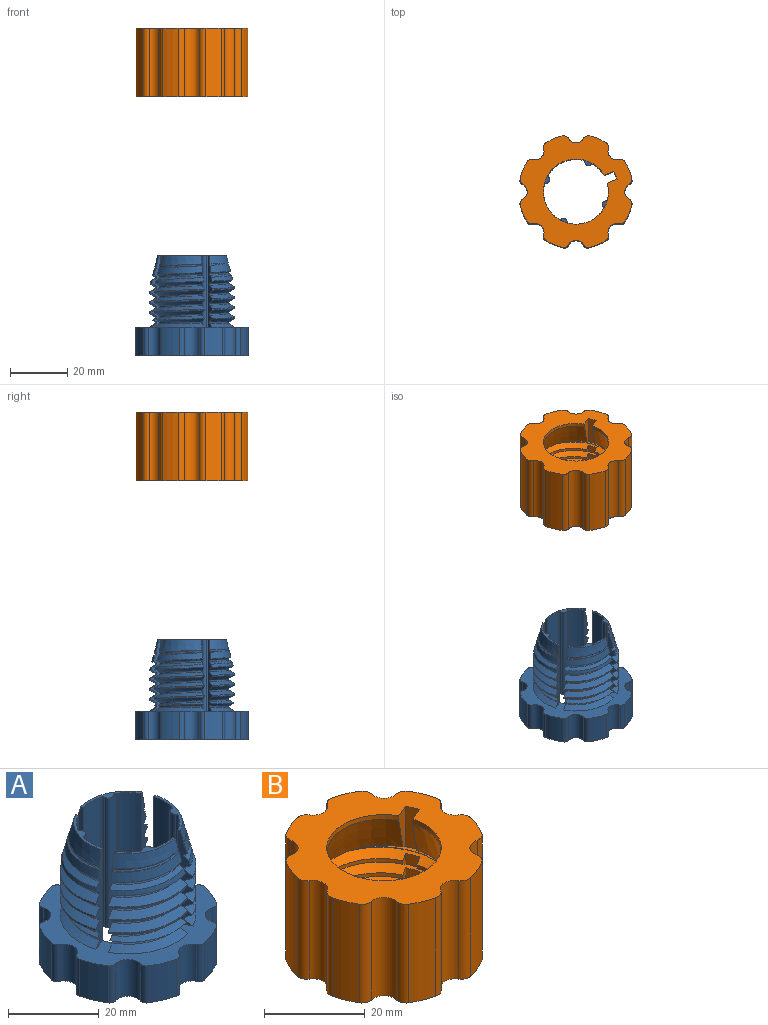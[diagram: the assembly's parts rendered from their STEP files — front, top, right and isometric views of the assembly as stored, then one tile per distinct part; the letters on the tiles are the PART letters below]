
ASSEMBLY  parts=2 mates=1
PART A: 173 faces, bbox 39.3x39.3x35 mm
  f0: cylinder r=11.39mm len=35mm, axis (0,0,-1), area 193.1mm2, adj f6,f127,f152,f166
  f1: cylinder r=11.39mm len=35mm, axis (0,0,-1), area 416.3mm2, adj f4,f5,f6,f127,f158,f159,f165,f168
  f2: cylinder r=11.39mm len=35mm, axis (0,0,-1), area 416.3mm2, adj f4,f5,f57,f127,f156,f157,f167,f170
  f3: cylinder r=11.39mm len=35mm, axis (0,0,-1), area 416.3mm2, adj f4,f57,f87,f127,f154,f155,f169,f172
  f4: plane 39.23x39.23mm, normal (0,0,1), area 475.3mm2, adj f1,f2,f3,f51,f52,f84,f112,f119
  f5: plane 13.6x6.3mm, normal (0,0,1), area 12mm2, adj f1,f2,f17,f157,f158,f163,f167,f168
  f6: plane 13.6x6.3mm, normal (0,0,1), area 12mm2, adj f0,f1,f18,f152,f159,f164,f165,f166
  f7: cylinder r=15mm len=17.54mm, axis (0,0,1), area 9mm2, adj f25,f45,f157,f158
  f8: cylinder r=15mm len=17.54mm, axis (0,0,1), area 7.3mm2, adj f26,f46,f116,f152,f159
  f9: cylinder r=15mm len=17.54mm, axis (0,0,1), area 9mm2, adj f23,f43,f157,f158
  f10: cylinder r=15mm len=17.54mm, axis (0,0,1), area 9mm2, adj f24,f44,f152,f159
  f11: cylinder r=15mm len=17.54mm, axis (0,0,1), area 9mm2, adj f21,f41,f157,f158
  f12: cylinder r=15mm len=17.54mm, axis (0,0,1), area 9mm2, adj f22,f42,f152,f159
  f13: cylinder r=11.39mm len=35mm, axis (0,0,-1), area 193.1mm2, adj f87,f127,f153,f171
  f14: cone r=12mm half-angle=15deg, axis (0,0,-1), area 24.3mm2, adj f27,f47,f157,f158
  f15: cone r=12mm half-angle=15deg, axis (0,0,-1), area 29.3mm2, adj f28,f48,f152,f159
  f16: cone r=12mm half-angle=15deg, axis (0,0,-1), area 43.1mm2, adj f39,f49,f70,f157,f158
  f17: cone r=12mm half-angle=15deg, axis (0,0,-1), area 56.2mm2, adj f5,f39,f83,f157,f158
  f18: cone r=12mm half-angle=15deg, axis (0,0,-1), area 95.4mm2, adj f6,f40,f50,f152,f159
  f19: bspline ~22.5x17.32mm, area 31.8mm2, adj f29,f55,f157,f158
  f20: bspline ~30.31x22.5mm, area 44.5mm2, adj f30,f56,f115,f152,f159
  f21: bspline ~17.54x8.87mm, area 44.9mm2, adj f11,f31,f157,f158
  f22: bspline ~30.31x22.5mm, area 44.9mm2, adj f12,f32,f152,f159
  f23: bspline ~17.54x8.87mm, area 44.9mm2, adj f9,f33,f157,f158
  f24: bspline ~30.31x22.5mm, area 44.9mm2, adj f10,f34,f152,f159
  f25: bspline ~22.5x17.32mm, area 44.9mm2, adj f7,f35,f157,f158
  f26: bspline ~30.31x22.5mm, area 44.3mm2, adj f8,f36,f116,f152,f159
  f27: bspline ~22.5x17.32mm, area 25.9mm2, adj f14,f37,f157,f158
  f28: bspline ~30.31x22.5mm, area 19.9mm2, adj f15,f38,f152,f159
  f29: bspline ~19.42x14.95mm, area 14.4mm2, adj f19,f41,f157,f158
  f30: bspline ~26.16x19.42mm, area 14.4mm2, adj f20,f42,f152,f159
  f31: bspline ~19.42x14.95mm, area 14.4mm2, adj f21,f43,f157,f158
  f32: bspline ~26.16x19.42mm, area 14.4mm2, adj f22,f44,f152,f159
  f33: bspline ~19.42x14.95mm, area 14.4mm2, adj f23,f45,f157,f158
  f34: bspline ~26.16x19.42mm, area 14.4mm2, adj f24,f46,f152,f159
  f35: bspline ~19.42x14.95mm, area 14.4mm2, adj f25,f47,f157,f158
  f36: bspline ~26.16x19.42mm, area 14.4mm2, adj f26,f48,f152,f159
  f37: bspline ~19.42x14.95mm, area 14.4mm2, adj f27,f49,f157,f158
  f38: bspline ~26.16x19.42mm, area 14.4mm2, adj f28,f50,f152,f159
  f39: bspline ~19.42x14.95mm, area 12.8mm2, adj f16,f17,f70,f83,f157,f158
  f40: bspline ~19.42x14.95mm, area 2.5mm2, adj f18,f159
  f41: bspline ~22.5x17.32mm, area 44.9mm2, adj f11,f29,f157,f158
  f42: bspline ~17.54x8.87mm, area 44.9mm2, adj f12,f30,f152,f159
  f43: bspline ~22.5x17.32mm, area 44.9mm2, adj f9,f31,f157,f158
  f44: bspline ~17.54x8.87mm, area 44.9mm2, adj f10,f32,f152,f159
  f45: bspline ~22.5x17.32mm, area 44.9mm2, adj f7,f33,f157,f158
  f46: bspline ~30.31x22.5mm, area 44.9mm2, adj f8,f34,f152,f159
  f47: bspline ~22.5x17.32mm, area 33.2mm2, adj f14,f35,f157,f158
  f48: bspline ~30.31x22.5mm, area 28.6mm2, adj f15,f36,f152,f159
  f49: bspline ~22.5x17.32mm, area 15.3mm2, adj f16,f37,f157,f158
  f50: bspline ~30.31x22.5mm, area 11mm2, adj f18,f38,f152,f159
  f51: cone r=15mm half-angle=60deg, axis (0,0,-1), area 44.9mm2, adj f4,f53,f157,f158
  f52: cone r=15mm half-angle=60deg, axis (0,0,-1), area 44.9mm2, adj f4,f54,f152,f159
  f53: torus R=13.15mm, axis (0,0,1), area 14.4mm2, adj f51,f55,f157,f158
  f54: torus R=13.15mm, axis (0,0,1), area 13mm2, adj f52,f56,f117,f152,f159
  f55: cone r=12.95mm half-angle=60deg, axis (0,0,1), area 31.8mm2, adj f19,f53,f157,f158
  f56: cone r=12.95mm half-angle=60deg, axis (0,0,1), area 35.1mm2, adj f20,f54,f115,f118,f159
  f57: plane 13.6x6.3mm, normal (0,0,1), area 12mm2, adj f2,f3,f63,f155,f156,f162,f169,f170
  f58: cylinder r=15mm len=17.54mm, axis (0,0,1), area 9mm2, adj f67,f79,f155,f156
  f59: cylinder r=15mm len=17.54mm, axis (0,0,1), area 9mm2, adj f66,f78,f155,f156
  f60: cylinder r=15mm len=17.54mm, axis (0,0,1), area 9mm2, adj f65,f77,f155,f156
  f61: cone r=12mm half-angle=15deg, axis (0,0,-1), area 19.1mm2, adj f68,f80,f155,f156
  f62: cone r=12mm half-angle=15deg, axis (0,0,-1), area 38.7mm2, adj f69,f81,f155,f156
  f63: cone r=12mm half-angle=15deg, axis (0,0,-1), area 69.4mm2, adj f57,f82,f155,f156
  f64: bspline ~30.31x22.5mm, area 15mm2, adj f71,f86,f155,f156
  f65: bspline ~30.31x22.5mm, area 44.9mm2, adj f60,f72,f155,f156
  f66: bspline ~30.31x22.5mm, area 44.9mm2, adj f59,f73,f155,f156
  f67: bspline ~30.31x22.5mm, area 44.9mm2, adj f58,f74,f155,f156
  f68: bspline ~30.31x22.5mm, area 32.2mm2, adj f61,f75,f155,f156
  f69: bspline ~30.31x22.5mm, area 8.1mm2, adj f62,f76,f155,f156
  f70: bspline ~22.5x17.32mm, area 2.4mm2, adj f16,f39,f157
  f71: bspline ~26.16x19.42mm, area 14.4mm2, adj f64,f77,f155,f156
  f72: bspline ~26.16x19.42mm, area 14.4mm2, adj f65,f78,f155,f156
  f73: bspline ~26.16x19.42mm, area 14.4mm2, adj f66,f79,f155,f156
  f74: bspline ~26.16x19.42mm, area 14.4mm2, adj f67,f80,f155,f156
  f75: bspline ~26.16x19.42mm, area 14.4mm2, adj f68,f81,f155,f156
  f76: bspline ~26.16x19.42mm, area 14.4mm2, adj f69,f82,f155,f156
  f77: bspline ~30.31x22.5mm, area 44.9mm2, adj f60,f71,f155,f156
  f78: bspline ~30.31x22.5mm, area 44.9mm2, adj f59,f72,f155,f156
  f79: bspline ~30.31x22.5mm, area 44.9mm2, adj f58,f73,f155,f156
  f80: bspline ~30.31x22.5mm, area 37.9mm2, adj f61,f74,f155,f156
  f81: bspline ~30.31x22.5mm, area 19.7mm2, adj f62,f75,f155,f156
  f82: bspline ~30.31x22.5mm, area 2.6mm2, adj f63,f76,f155,f156
  f83: bspline ~12.99x8.53mm, area 0mm2, adj f17,f39,f157
  f84: cone r=15mm half-angle=60deg, axis (0,0,-1), area 44.9mm2, adj f4,f85,f155,f156
  f85: torus R=13.15mm, axis (0,0,1), area 14.4mm2, adj f84,f86,f155,f156
  f86: cone r=12.95mm half-angle=60deg, axis (0,0,1), area 15mm2, adj f64,f85,f155,f156
  f87: plane 13.6x6.3mm, normal (0,0,1), area 12mm2, adj f3,f13,f93,f153,f154,f161,f171,f172
  f88: cylinder r=15mm len=17.54mm, axis (0,0,1), area 9mm2, adj f97,f108,f153,f154
  f89: cylinder r=15mm len=17.54mm, axis (0,0,1), area 9mm2, adj f96,f107,f153,f154
  f90: cylinder r=15mm len=17.54mm, axis (0,0,1), area 9mm2, adj f95,f106,f153,f154
  f91: cone r=12mm half-angle=15deg, axis (0,0,-1), area 13.6mm2, adj f98,f109,f153,f154
  f92: cone r=12mm half-angle=15deg, axis (0,0,-1), area 34.2mm2, adj f99,f110,f153,f154
  f93: cone r=12mm half-angle=15deg, axis (0,0,-1), area 83.2mm2, adj f87,f111,f153,f154
  f94: bspline ~15x6.11mm, area 1.3mm2, adj f100,f114,f154
  f95: bspline ~22.5x17.32mm, area 44.9mm2, adj f90,f101,f153,f154
  f96: bspline ~22.5x17.32mm, area 44.9mm2, adj f89,f102,f153,f154
  f97: bspline ~22.5x17.32mm, area 44.9mm2, adj f88,f103,f153,f154
  f98: bspline ~22.5x17.32mm, area 38.5mm2, adj f91,f104,f153,f154
  f99: bspline ~22.5x17.32mm, area 13.9mm2, adj f92,f105,f153,f154
  f100: bspline ~19.42x14.95mm, area 13.1mm2, adj f94,f106,f113,f153,f154
  f101: bspline ~19.42x14.95mm, area 14.4mm2, adj f95,f107,f153,f154
  f102: bspline ~19.42x14.95mm, area 14.4mm2, adj f96,f108,f153,f154
  f103: bspline ~19.42x14.95mm, area 14.4mm2, adj f97,f109,f153,f154
  f104: bspline ~19.42x14.95mm, area 14.4mm2, adj f98,f110,f153,f154
  f105: bspline ~19.42x14.95mm, area 14.4mm2, adj f99,f111,f153,f154
  f106: bspline ~22.5x17.32mm, area 44.9mm2, adj f90,f100,f153,f154
  f107: bspline ~22.5x17.32mm, area 44.9mm2, adj f89,f101,f153,f154
  f108: bspline ~22.5x17.32mm, area 44.9mm2, adj f88,f102,f153,f154
  f109: bspline ~22.5x17.32mm, area 42.6mm2, adj f91,f103,f153,f154
  f110: bspline ~22.5x17.32mm, area 24.1mm2, adj f92,f104,f153,f154
  f111: bspline ~22.5x17.32mm, area 6.7mm2, adj f93,f105,f153,f154
  f112: cone r=15mm half-angle=60deg, axis (0,0,-1), area 44.9mm2, adj f4,f113,f153,f154
  f113: torus R=13.15mm, axis (0,0,1), area 13mm2, adj f100,f112,f114,f153,f154
  f114: cone r=12.95mm half-angle=60deg, axis (0,0,1), area 1.3mm2, adj f94,f113,f154
  f115: cylinder r=15mm len=14.84mm, axis (0,0,1), area 4.4mm2, adj f20,f56,f118,f152
  f116: cone r=12mm half-angle=15deg, axis (0,0,-1), area 2.1mm2, adj f8,f26,f152
  f117: bspline ~11.21x6.62mm, area 1.6mm2, adj f54,f118,f152
  f118: bspline ~12.99x8.53mm, area 9.4mm2, adj f56,f115,f117,f152
  f119: cylinder r=20.07mm len=10mm, axis (0,0,1), area 69.1mm2, adj f4,f127,f136,f151
  f120: cylinder r=20.07mm len=10mm, axis (0,0,1), area 69.1mm2, adj f4,f127,f137,f138
  f121: cylinder r=20.07mm len=10mm, axis (0,0,1), area 69.1mm2, adj f4,f127,f139,f140
  f122: cylinder r=20.07mm len=10mm, axis (0,0,1), area 69.1mm2, adj f4,f127,f141,f142
  f123: cylinder r=20.07mm len=10mm, axis (0,0,1), area 69.1mm2, adj f4,f127,f143,f144
  f124: cylinder r=20.07mm len=10mm, axis (0,0,1), area 69.1mm2, adj f4,f127,f145,f146
  f125: cylinder r=20.07mm len=10mm, axis (0,0,1), area 69.1mm2, adj f4,f127,f147,f148
  f126: cylinder r=20.07mm len=10mm, axis (0,0,1), area 69.1mm2, adj f4,f127,f149,f150
  f127: plane 39.23x39.23mm, normal (0,0,-1), area 741.6mm2, adj f0,f1,f2,f3,f13,f119,f120,f121
  f128: cylinder r=3mm len=10mm, axis (0,0,-1), area 67.5mm2, adj f4,f127,f150,f151
  f129: cylinder r=3mm len=10mm, axis (0,0,-1), area 67.5mm2, adj f4,f127,f148,f149
  f130: cylinder r=3mm len=10mm, axis (0,0,-1), area 67.5mm2, adj f4,f127,f146,f147
  f131: cylinder r=3mm len=10mm, axis (0,0,-1), area 67.5mm2, adj f4,f127,f144,f145
  f132: cylinder r=3mm len=10mm, axis (0,0,-1), area 67.5mm2, adj f4,f127,f142,f143
  f133: cylinder r=3mm len=10mm, axis (0,0,-1), area 67.5mm2, adj f4,f127,f140,f141
  f134: cylinder r=3mm len=10mm, axis (0,0,-1), area 67.5mm2, adj f4,f127,f138,f139
  f135: cylinder r=3mm len=10mm, axis (0,0,-1), area 67.5mm2, adj f4,f127,f136,f137
  f136: cylinder r=1.5mm len=10mm, axis (0,0,-1), area 20.2mm2, adj f4,f119,f127,f135
  f137: cylinder r=1.5mm len=10mm, axis (0,0,1), area 20.2mm2, adj f4,f120,f127,f135
  f138: cylinder r=1.5mm len=10mm, axis (0,0,-1), area 20.2mm2, adj f4,f120,f127,f134
  f139: cylinder r=1.5mm len=10mm, axis (0,0,1), area 20.2mm2, adj f4,f121,f127,f134
  f140: cylinder r=1.5mm len=10mm, axis (0,0,-1), area 20.2mm2, adj f4,f121,f127,f133
  f141: cylinder r=1.5mm len=10mm, axis (0,0,1), area 20.2mm2, adj f4,f122,f127,f133
  f142: cylinder r=1.5mm len=10mm, axis (0,0,-1), area 20.2mm2, adj f4,f122,f127,f132
  f143: cylinder r=1.5mm len=10mm, axis (0,0,1), area 20.2mm2, adj f4,f123,f127,f132
  f144: cylinder r=1.5mm len=10mm, axis (0,0,-1), area 20.2mm2, adj f4,f123,f127,f131
  f145: cylinder r=1.5mm len=10mm, axis (0,0,1), area 20.2mm2, adj f4,f124,f127,f131
  f146: cylinder r=1.5mm len=10mm, axis (0,0,-1), area 20.2mm2, adj f4,f124,f127,f130
  f147: cylinder r=1.5mm len=10mm, axis (0,0,1), area 20.2mm2, adj f4,f125,f127,f130
  f148: cylinder r=1.5mm len=10mm, axis (0,0,-1), area 20.2mm2, adj f4,f125,f127,f129
  f149: cylinder r=1.5mm len=10mm, axis (0,0,1), area 20.2mm2, adj f4,f126,f127,f129
  f150: cylinder r=1.5mm len=10mm, axis (0,0,-1), area 20.2mm2, adj f4,f126,f127,f128
  f151: cylinder r=1.5mm len=10mm, axis (0,0,1), area 20.2mm2, adj f4,f119,f127,f128
  f152: plane 35.05x3.48mm, normal (-0.38,0.92,0), area 91.6mm2, adj f0,f4,f6,f8,f10,f12,f15,f18
  f153: plane 35.05x3.48mm, normal (0.38,-0.92,0), area 91.4mm2, adj f4,f13,f87,f88,f89,f90,f91,f92
  f154: plane 25.05x3.41mm, normal (-0.92,-0.38,0), area 53.5mm2, adj f3,f4,f87,f88,f89,f90,f91,f92
  f155: plane 25.05x3.41mm, normal (0.92,0.38,0), area 53.5mm2, adj f3,f4,f57,f58,f59,f60,f61,f62
  f156: plane 25.05x3.41mm, normal (0.38,-0.92,0), area 53.3mm2, adj f2,f4,f57,f58,f59,f60,f61,f62
  f157: plane 25.05x3.41mm, normal (-0.38,0.92,0), area 53.4mm2, adj f2,f4,f5,f7,f9,f11,f14,f16
  f158: plane 25.05x3.41mm, normal (0.92,0.38,0), area 53.8mm2, adj f1,f4,f5,f7,f9,f11,f14,f16
  f159: plane 25.05x3.41mm, normal (-0.92,-0.38,0), area 53.9mm2, adj f1,f4,f6,f8,f10,f12,f15,f18
  f160: plane 10x2.77mm, normal (-0.92,-0.38,0), area 30mm2, adj f4,f127,f152,f153
  f161: cylinder r=1.25mm len=35mm, axis (0,0,-1), area 96.6mm2, adj f87,f127,f171,f172
  f162: cylinder r=1.25mm len=35mm, axis (0,0,-1), area 96.6mm2, adj f57,f127,f169,f170
  f163: cylinder r=1.25mm len=35mm, axis (0,0,-1), area 96.6mm2, adj f5,f127,f167,f168
  f164: cylinder r=1.25mm len=35mm, axis (0,0,-1), area 96.6mm2, adj f6,f127,f165,f166
  f165: cylinder r=0.75mm len=35mm, axis (0,0,-1), area 33.4mm2, adj f1,f6,f127,f164
  f166: cylinder r=0.75mm len=35mm, axis (0,0,-1), area 33.4mm2, adj f0,f6,f127,f164
  f167: cylinder r=0.75mm len=35mm, axis (0,0,-1), area 33.4mm2, adj f2,f5,f127,f163
  f168: cylinder r=0.75mm len=35mm, axis (0,0,-1), area 33.4mm2, adj f1,f5,f127,f163
  f169: cylinder r=0.75mm len=35mm, axis (0,0,-1), area 33.4mm2, adj f3,f57,f127,f162
  f170: cylinder r=0.75mm len=35mm, axis (0,0,-1), area 33.4mm2, adj f2,f57,f127,f162
  f171: cylinder r=0.75mm len=35mm, axis (0,0,-1), area 33.4mm2, adj f13,f87,f127,f161
  f172: cylinder r=0.75mm len=35mm, axis (0,0,-1), area 33.4mm2, adj f3,f87,f127,f161
PART B: 63 faces, bbox 40.3x40.3x26.7 mm
  f0: plane 39.06x39.06mm, normal (0,0,1), area 728mm2, adj f3,f13,f14,f15,f16,f17,f18,f19
  f1: bspline ~36.09x31.26mm, area 816.8mm2, adj f5,f6,f7,f8,f12,f21,f23,f51
  f2: bspline ~13.54x8.88mm, area 0.6mm2, adj f9,f12,f61
  f3: cylinder r=11.39mm len=22.77mm, axis (0,0,1), area 74.9mm2, adj f0,f4,f49,f50
  f4: cone r=11.39mm half-angle=15deg, axis (0,0,-1), area 615.4mm2, adj f3,f11,f49,f50
  f5: cylinder r=13.51mm len=25.33mm, axis (0,0,1), area 24.5mm2, adj f1,f10,f23,f53
  f6: cylinder r=13.51mm len=27.01mm, axis (0,0,1), area 71.6mm2, adj f1,f10,f52,f56
  f7: cylinder r=13.51mm len=27.01mm, axis (0,0,1), area 71.6mm2, adj f1,f10,f55,f59
  f8: cylinder r=13.51mm len=27.01mm, axis (0,0,1), area 71.6mm2, adj f1,f10,f58,f60
  f9: cylinder r=13.51mm len=17.26mm, axis (0,0,1), area 12.6mm2, adj f2,f10,f12,f61
  f10: bspline ~36.09x31.26mm, area 813.1mm2, adj f5,f6,f7,f8,f9,f12,f21,f23
  f11: cone r=13.51mm half-angle=60deg, axis (0,0,-1), area 219.2mm2, adj f4,f22,f48,f49,f50
  f12: plane 40.33x40.33mm, normal (0,0,-1), area 493.6mm2, adj f1,f2,f9,f10,f13,f14,f15,f16
  f13: cylinder r=20.07mm len=24mm, axis (0,0,1), area 141.9mm2, adj f0,f12,f32,f47
  f14: cylinder r=20.07mm len=24mm, axis (0,0,1), area 141.9mm2, adj f0,f12,f33,f34
  f15: cylinder r=20.07mm len=24mm, axis (0,0,1), area 141.9mm2, adj f0,f12,f35,f36
  f16: cylinder r=20.07mm len=24mm, axis (0,0,1), area 141.9mm2, adj f0,f12,f37,f38
  f17: cylinder r=20.07mm len=24mm, axis (0,0,1), area 141.9mm2, adj f0,f12,f39,f40
  f18: cylinder r=20.07mm len=24mm, axis (0,0,1), area 141.9mm2, adj f0,f12,f41,f42
  f19: cylinder r=20.07mm len=24mm, axis (0,0,1), area 141.9mm2, adj f0,f12,f43,f44
  f20: cylinder r=20.07mm len=24mm, axis (0,0,1), area 141.9mm2, adj f0,f12,f45,f46
  f21: bspline ~36.27x31.41mm, area 80.3mm2, adj f1,f10,f12,f22,f23
  f22: revolved ~31.35x31.35mm, area 20.5mm2, adj f11,f21,f23
  f23: cone r=15.63mm half-angle=60deg, axis (0,0,1), area 137.1mm2, adj f1,f5,f10,f21,f22
  f24: cylinder r=3mm len=24mm, axis (0,0,-1), area 147.9mm2, adj f0,f12,f46,f47
  f25: cylinder r=3mm len=24mm, axis (0,0,-1), area 147.9mm2, adj f0,f12,f44,f45
  f26: cylinder r=3mm len=24mm, axis (0,0,-1), area 147.9mm2, adj f0,f12,f42,f43
  f27: cylinder r=3mm len=24mm, axis (0,0,-1), area 147.9mm2, adj f0,f12,f40,f41
  f28: cylinder r=3mm len=24mm, axis (0,0,-1), area 147.9mm2, adj f0,f12,f38,f39
  f29: cylinder r=3mm len=24mm, axis (0,0,-1), area 147.9mm2, adj f0,f12,f36,f37
  f30: cylinder r=3mm len=24mm, axis (0,0,-1), area 147.9mm2, adj f0,f12,f34,f35
  f31: cylinder r=3mm len=24mm, axis (0,0,-1), area 147.9mm2, adj f0,f12,f32,f33
  f32: cylinder r=2.1mm len=24mm, axis (0,0,-1), area 64.1mm2, adj f0,f12,f13,f31
  f33: cylinder r=2.1mm len=24mm, axis (0,0,1), area 64.1mm2, adj f0,f12,f14,f31
  f34: cylinder r=2.1mm len=24mm, axis (0,0,-1), area 64.1mm2, adj f0,f12,f14,f30
  f35: cylinder r=2.1mm len=24mm, axis (0,0,1), area 64.1mm2, adj f0,f12,f15,f30
  f36: cylinder r=2.1mm len=24mm, axis (0,0,-1), area 64.1mm2, adj f0,f12,f15,f29
  f37: cylinder r=2.1mm len=24mm, axis (0,0,1), area 64.1mm2, adj f0,f12,f16,f29
  f38: cylinder r=2.1mm len=24mm, axis (0,0,-1), area 64.1mm2, adj f0,f12,f16,f28
  f39: cylinder r=2.1mm len=24mm, axis (0,0,1), area 64.1mm2, adj f0,f12,f17,f28
  f40: cylinder r=2.1mm len=24mm, axis (0,0,-1), area 64.1mm2, adj f0,f12,f17,f27
  f41: cylinder r=2.1mm len=24mm, axis (0,0,1), area 64.1mm2, adj f0,f12,f18,f27
  f42: cylinder r=2.1mm len=24mm, axis (0,0,-1), area 64.1mm2, adj f0,f12,f18,f26
  f43: cylinder r=2.1mm len=24mm, axis (0,0,1), area 64.1mm2, adj f0,f12,f19,f26
  f44: cylinder r=2.1mm len=24mm, axis (0,0,-1), area 64.1mm2, adj f0,f12,f19,f25
  f45: cylinder r=2.1mm len=24mm, axis (0,0,1), area 64.1mm2, adj f0,f12,f20,f25
  f46: cylinder r=2.1mm len=24mm, axis (0,0,-1), area 64.1mm2, adj f0,f12,f20,f24
  f47: cylinder r=2.1mm len=24mm, axis (0,0,1), area 64.1mm2, adj f0,f12,f13,f24
  f48: plane 9.86x2.77mm, normal (-0.92,-0.38,0), area 29.5mm2, adj f0,f11,f49,f50
  f49: plane 9.88x3.38mm, normal (-0.38,0.92,0), area 24.9mm2, adj f0,f3,f4,f11,f48
  f50: plane 9.88x3.38mm, normal (0.38,-0.92,0), area 24.9mm2, adj f0,f3,f4,f11,f48
  f51: plane 2.94x2.89mm, normal (-0.92,-0.38,0), area 7.6mm2, adj f1,f10,f52,f53
  f52: plane 2.61x1.4mm, normal (-0.38,0.92,0), area 2.6mm2, adj f1,f6,f10,f51
  f53: plane 2.61x1.4mm, normal (0.38,-0.92,0), area 2.6mm2, adj f1,f5,f10,f51
  f54: plane 2.94x2.89mm, normal (-0.92,-0.38,0), area 7.6mm2, adj f1,f10,f55,f56
  f55: plane 2.61x1.4mm, normal (-0.38,0.92,0), area 2.6mm2, adj f1,f7,f10,f54
  f56: plane 2.61x1.4mm, normal (0.38,-0.92,0), area 2.6mm2, adj f1,f6,f10,f54
  f57: plane 2.94x2.89mm, normal (-0.92,-0.38,0), area 7.6mm2, adj f1,f10,f58,f59
  f58: plane 2.61x1.4mm, normal (-0.38,0.92,0), area 2.6mm2, adj f1,f8,f10,f57
  f59: plane 2.61x1.4mm, normal (0.38,-0.92,0), area 2.6mm2, adj f1,f7,f10,f57
  f60: plane 2.02x1.4mm, normal (0.38,-0.92,0), area 2.3mm2, adj f1,f8,f10,f12,f62
  f61: plane 1.9x1.4mm, normal (-0.38,0.92,0), area 2.2mm2, adj f2,f9,f10,f12,f62
  f62: plane 2.94x2.18mm, normal (-0.92,-0.38,0), area 5.8mm2, adj f10,f12,f60,f61
PLACE A rot(axis=(-0.08,-0.99,0.12),0deg) t=(-18.82,-98.33,34.25)mm
PLACE B rot(axis=(-0.08,-0.99,0.12),0deg) t=(-18.82,-98.33,124.77)mm
MATE slider A.f0 <-> B.f3  axis (0,0,1) through (-18.82,-98.33,39.25)mm
